# Revit family: BIMLIB_Термостатический_клапан_TVD_РОСТерм
name_source: partatom
category: Арматура трубопроводов
revit_build: Autodesk Revit 2017 (Build: 20170118_1100(x64)
units: mm (PartAtom-declared; Revit-internal decimal feet)

## family parameters
Всегда вертикально = Нет
На основе рабочей плоскости = Нет
Общий = Нет
При загрузке вырезать с полостями = Нет
Размер круглого соединителя = Использовать диаметр
Тип детали = Клапан - Вставляется

## types (1)
- HEIZEN TVD
    ADSK_URL документации изделия = http://rostherm.ru
    ADSK_URL страницы изделия = http://rostherm.ru
    ADSK_Версия Revit = 2017
    ADSK_Единица измерения = шт.
    ADSK_Завод-изготовитель = Heizen
    ADSK_Код изделия = TVD 2101-15
    ADSK_Марка = TVD 2101 Ду15
    ADSK_Масса = 0
    ADSK_Наименование = ТЕРМОСТАТИЧЕСКИЙ КЛАПАН С ПРЕДВАРИТЕЛЬНОЙ НАСТРОЙКОЙ TVD 2101 Ду15
    ADSK_Наименование краткое = TVD 2101 Ду15
    ADSK_Обозначение = ГОСТ 30815-2002
    BL_BIM library = https://bimlib.pro
    URL = http://rostherm.ru
    Изготовитель = РОСТерм
    Коэффициент K = 0
    Метод определения потерь = Не задано
    Описание = Термостатические клапаны предназначены для автоматического или ручного регулирования расхода теплоносителя с температурой до 120ºС
и рабочим давлением до 1,0 МПа включительно через отопительный
прибор водяной системы отопления.
    РТ_DN = 15 мм
    РТ_L = 95 мм
    РТ_Номинальное давление = 10.0 бары

## geometry (parser evidence)
native form markers: Sweep x1
no freeform markers — native parametric forms only
